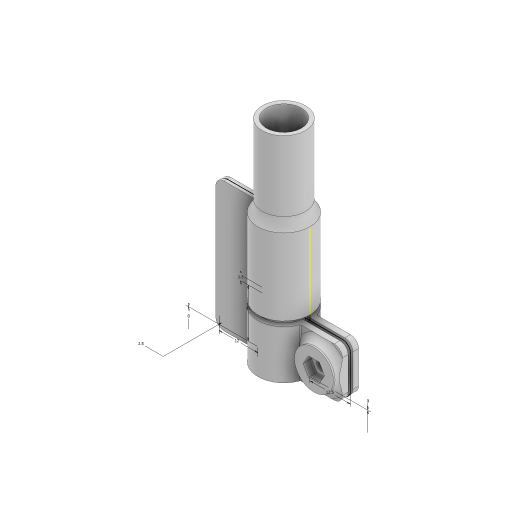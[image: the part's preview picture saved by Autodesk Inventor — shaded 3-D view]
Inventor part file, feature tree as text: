
AUTODESK INVENTOR PART (.ipt)
format: ipt  version: 2023 (Build 270158000, 158)  size: 264,704 bytes
history: native  units: mm
features: extrude x8, sketch x6, fillet x5, chamfer x1
ambient origin geometry x8: Origin, YZ Plane, XZ Plane, XY Plane, X Axis, Y Axis, Z Axis, Center Point
bodies: Solid1 (feature_tree)
feature tree (20):
  extrude  "Extrusion1"  Depth=16.0mm
  extrude  "Extrusion2"  Depth=40.0mm TaperAngle=0.0deg
  fillet  "Fillet1"  Radius=13.3mm
  fillet  "Fillet2"  Radius=10.8mm
  sketch  "Sketch3"  dims[d7=25.0mm d8=0.0mm d9=5.0mm]
  extrude  "Extrusion3"  Depth=5.0mm
  extrude  "Extrusion4"  Depth=12.0mm
  extrude  "Extrusion5"  Depth=15.0mm
  extrude  "Extrusion6"  TaperAngle=0.0deg  [1 undecoded]
  fillet  "Fillet3"  Radius=12.5mm
  fillet  "Fillet4"  Radius=2.5mm
  extrude  "Extrusion7"  Depth=0.5mm TaperAngle=0.0deg
  fillet  "Fillet6"  Radius=5.0mm
  extrude  "Extrusion8"  Depth=0.5mm
  chamfer  "Chamfer1"  Distance=0.75mm
  sketch  "Sketch1"  dims[d0=13.1mm d1=16.0mm]
  sketch  "Sketch2"  dims[d2=1.45mm d3=40.0mm d4=0.0mm d5=13.3mm d6=10.8mm]
  sketch  "Sketch4"  dims[d10=3.0mm d11=12.0mm]
  sketch  "Sketch5"  dims[d12=0.0mm d13=15.0mm]
  sketch  "Sketch6"  dims[d14=1.5mm d15=0.0mm d16=12.5mm d17=2.5mm d18=2.0mm d19=0.0mm d20=5.0mm d21=0.0mm d22=1.5mm d23=0.75mm d24=15.0mm d25=0.0mm d26=0.0mm d27=0.0mm d28=0.5mm d29=0.5mm d30=12.0mm d31=6.25mm d32=15.0mm d33=7.5mm d34=5.7mm d35=2.5mm d36=0.0mm d38=3.5mm d39=0.0mm d40=0.0mm d41=1.0mm d42=2.0mm d43=45.0deg d44=2.0mm]
note: 1 required parameter value undecoded (feature->parameter linkage not recoverable at this tier; creation-order binding heuristic only, values carry confidence <= 0.55)
